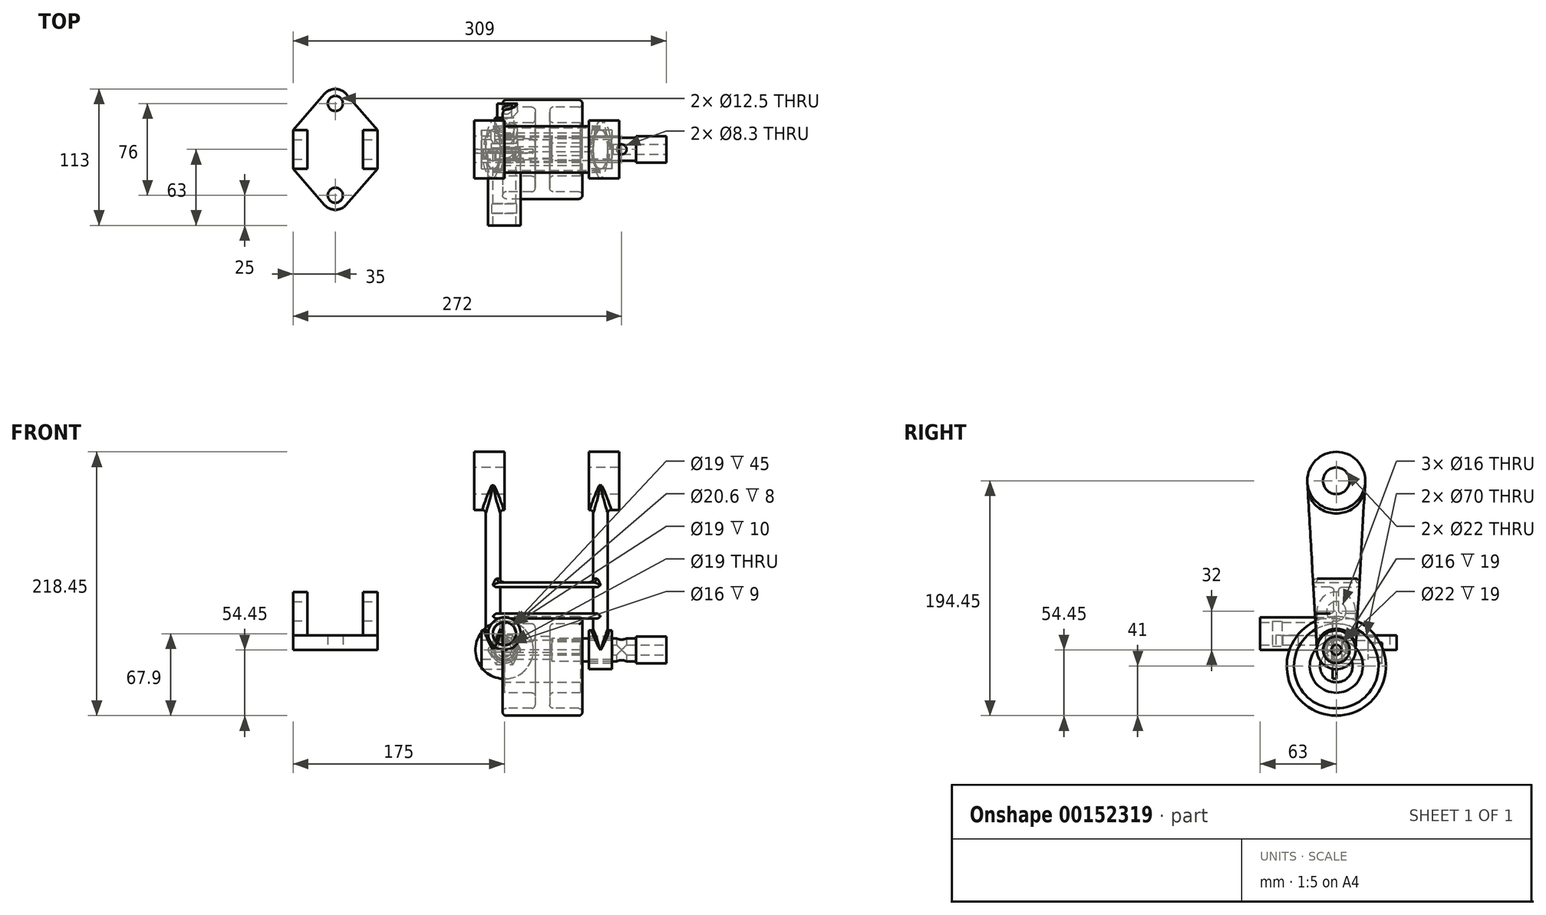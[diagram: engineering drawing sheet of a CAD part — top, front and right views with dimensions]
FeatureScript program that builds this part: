
annotation { "Feature Type Name" : "Feature", "Feature Type Description" : "" }
export const myFeature = defineFeature(function(context is Context, id is Id, definition is map)
    precondition{}
    {
        {
            assignVariable(context, id + "F0", {"name" : "gap", "anyValue" : 70});
        }
        {
            var Q0;
            Q0=qCreatedBy(makeId("Right.planeOp"),FACE);
            var sketch = newSketch(context, id + "F1", { "sketchPlane" : qUnion([Q0])});
            skCircle(sketch, "E0", {"center": v(0, 0) * mm, "radius": 16 * mm});
            skCircle(sketch, "E1", {"center": v(0, 140) * mm, "radius": 24 * mm});
            skSolve(sketch);
        }
        {
            var Q0;
            Q0=makeQuery(id+"F1.imprint","IMPRINT",FACE,{"disambiguationData":[TD([[makeQuery(id+"F1.imprint","IMPRINT",EDGE,{"derivedFrom":sQuery(id+"F1.wireOp",EDGE,"E1")}),1.0]])]});
            extrude(context, id + "F2", {"entities" : qUnion([Q0]), "oppositeDirection" : true, "depth" : 25 * mm});
        }
        {
            var Q0;
            Q0=makeQuery(id+"F1.imprint","IMPRINT",FACE,{"disambiguationData":[TD([[makeQuery(id+"F1.imprint","IMPRINT",EDGE,{"derivedFrom":sQuery(id+"F1.wireOp",EDGE,"E0")}),1.0]])]});
            extrude(context, id + "F3", {"entities" : qUnion([Q0]), "oppositeDirection" : true, "depth" : 19 * mm});
        }
        {
            var Q0;
            Q0=qCreatedBy(makeId("Top.planeOp"),FACE);
            var sketch = newSketch(context, id + "F4", { "sketchPlane" : qUnion([Q0])});
            skEllipse(sketch, "E2", {"center": v(-9.5, 0) * mm, "majorRadius": 16 * mm, "minorRadius": 6 * mm, "majorAxis": v(0, 1)});
            skLineSegment(sketch, "E3", {"start": v(-19, 16) * mm, "end": v(0, 16) * mm, "construction": true});
            skPoint(sketch, "E4", {"position": v(-15.5, 0) * mm});
            skSolve(sketch);
        }
        {
            var Q0;
            Q0=sQuery(id+"F1.wireOp",VERTEX,"E1.center");
            var Q1;
            Q1=qCreatedBy(makeId("Top.planeOp"),FACE);
            cPlane(context, id + "F5", {"entities" : qUnion([Q0, Q1]), "cplaneType" : CPlaneType.PLANE_POINT, "offset" : 25 * mm, "width" : 150 * mm, "height" : 150 * mm});
        }
        {
            var Q0;
            Q0=qCreatedBy(id+"F5.planeOp",FACE);
            var sketch = newSketch(context, id + "F6", { "sketchPlane" : qUnion([Q0])});
            skLineSegment(sketch, "E5", {"start": v(-25, 24) * mm, "end": v(0, 24) * mm, "construction": true});
            skEllipse(sketch, "E6", {"center": v(-9.5, 0) * mm, "majorRadius": 24 * mm, "minorRadius": 6 * mm, "majorAxis": v(0, 1)});
            skSolve(sketch);
        }
        {
            var Q2;
            Q2=qSketchRegion(id+"F6",true);
            var Q3;
            Q3=qSketchRegion(id+"F4",true);
            loft(context, id + "F7", {"operationType" : NewBodyOperationType.ADD, "sheetProfilesArray" : [{ "sheetProfileEntities" : qUnion([Q2]) }, { "sheetProfileEntities" : qUnion([Q3]) }]});
        }
        {
            var Q0;
            Q0=makeQuery(id+"F2.opExtrude","SWEPT_BODY",BODY,{"disambiguationData":[OSD([sQuery(id+"F1.wireOp",EDGE,"E1")])]});
            transform(context, id + "F8", {"entities" : qUnion([Q0]), "transformType" : TransformType.TRANSLATION_3D, "dx" : (getVariable(context, 'gap')) * mm, "dy" : 0 * mm, "dz" : 0 * mm, "makeCopy" : true});
        }
        {
            var Q0;
            Q0=makeQuery(id+"F8.opPattern","COPY",FACE,{"derivedFrom":makeQuery(id+"F2.opExtrude","CAP_FACE",FACE,{"disambiguationData":[OSD([sQuery(id+"F1.wireOp",EDGE,"E1")])],"isStart":true}),"instanceName":"1"});
            var sketch = newSketch(context, id + "F9", { "sketchPlane" : qUnion([Q0])});
            skLineSegment(sketch, "E7", {"start": v(0, 140) * mm, "end": v(0, -24.66) * mm, "construction": true});
            skSolve(sketch);
        }
        {
            var Q0;
            Q0=makeQuery(id+"F8.opPattern","COPY",BODY,{"derivedFrom":makeQuery(id+"F2.opExtrude","SWEPT_BODY",BODY,{"disambiguationData":[OSD([sQuery(id+"F1.wireOp",EDGE,"E1")])]}),"instanceName":"1"});
            var Q1;
            Q1=sQuery(id+"F9.wireOp",EDGE,"E7");
            transform(context, id + "F10", {"entities" : qUnion([Q0]), "transformType" : TransformType.ROTATION, "transformAxis" : qUnion([Q1]), "angle" : 180 * degree, "makeCopy" : false});
        }
        {
            var Q0;
            Q0=qCreatedBy(makeId("Right.planeOp"),FACE);
            cPlane(context, id + "F11", {"entities" : qUnion([Q0]), "cplaneType" : CPlaneType.OFFSET, "offset" : 9.5 * mm, "oppositeDirection" : true, "width" : 150 * mm, "height" : 150 * mm});
        }
        {
            var Q0;
            Q0=qCreatedBy(id+"F11.planeOp",FACE);
            var sketch = newSketch(context, id + "F12", { "sketchPlane" : qUnion([Q0])});
            skCircle(sketch, "E8.0", {"center": v(0, 140) * mm, "radius": 24 * mm, "construction": true});
            skCircle(sketch, "E9.0", {"center": v(0, 0) * mm, "radius": 16 * mm, "construction": true});
            skLineSegment(sketch, "E10", {"start": v(-23.96, 138.63) * mm, "end": v(-15.97, -0.91) * mm, "construction": true});
            skLineSegment(sketch, "E11", {"start": v(23.96, 138.63) * mm, "end": v(15.97, -0.91) * mm, "construction": true});
            skLineSegment(sketch, "E12", {"start": v(15.63, 26) * mm, "end": v(-15.63, 26) * mm});
            skArc(sketch, "E13", {"start": v(-15.63, 30) * mm, "mid": v(-17.63, 28) * mm, "end": v(-15.63, 26) * mm});
            skArc(sketch, "E14", {"start": v(15.63, 26) * mm, "mid": v(17.63, 28) * mm, "end": v(15.63, 30) * mm});
            skLineSegment(sketch, "E15", {"start": v(-17.11, 56) * mm, "end": v(17.11, 56) * mm});
            skArc(sketch, "E16", {"start": v(-17.11, 56) * mm, "mid": v(-19.11, 54) * mm, "end": v(-17.11, 52) * mm});
            skArc(sketch, "E17", {"start": v(17.11, 52) * mm, "mid": v(19.11, 54) * mm, "end": v(17.11, 56) * mm});
            skLineSegment(sketch, "E18", {"start": v(-17.11, 52) * mm, "end": v(-5, 52) * mm});
            skLineSegment(sketch, "E19", {"start": v(-2, 49) * mm, "end": v(-2, 33) * mm});
            skLineSegment(sketch, "E20", {"start": v(-5, 30) * mm, "end": v(-15.63, 30) * mm});
            skLineSegment(sketch, "E21", {"start": v(17.11, 52) * mm, "end": v(5, 52) * mm});
            skLineSegment(sketch, "E22", {"start": v(2, 49) * mm, "end": v(2, 33) * mm});
            skLineSegment(sketch, "E23", {"start": v(5, 30) * mm, "end": v(15.63, 30) * mm});
            skPoint(sketch, "E24.visualSharp", {"position": v(-2, 52) * mm});
            skArc(sketch, "E24.filletArc", {"start": v(-2, 49) * mm, "mid": v(-2.88, 51.12) * mm, "end": v(-5, 52) * mm});
            skPoint(sketch, "E25.visualSharp", {"position": v(2, 52) * mm});
            skArc(sketch, "E25.filletArc", {"start": v(5, 52) * mm, "mid": v(2.88, 51.12) * mm, "end": v(2, 49) * mm});
            skPoint(sketch, "E26.visualSharp", {"position": v(2, 30) * mm});
            skArc(sketch, "E26.filletArc", {"start": v(2, 33) * mm, "mid": v(2.88, 30.88) * mm, "end": v(5, 30) * mm});
            skPoint(sketch, "E27.visualSharp", {"position": v(-2, 30) * mm});
            skArc(sketch, "E27.filletArc", {"start": v(-5, 30) * mm, "mid": v(-2.88, 30.88) * mm, "end": v(-2, 33) * mm});
            skSolve(sketch);
        }
        {
            var Q0;
            Q0=qSketchRegion(id+"F12",true);
            var Q1;
            Q1=makeQuery(id+"F8.opPattern","COPY",BODY,{"derivedFrom":makeQuery(id+"F2.opExtrude","SWEPT_BODY",BODY,{"disambiguationData":[OSD([sQuery(id+"F1.wireOp",EDGE,"E1")])]}),"instanceName":"1"});
            extrude(context, id + "F13", {"entities" : qUnion([Q0]), "operationType" : NewBodyOperationType.ADD, "endBoundEntityBody" : qUnion([Q1]), "depth" : (getVariable(context, 'gap') + 19) * mm});
        }
        {
            var Q0;
            Q0=qCreatedBy(makeId("Top.planeOp"),FACE);
            var sketch = newSketch(context, id + "F14", { "sketchPlane" : qUnion([Q0])});
            skLineSegment(sketch, "E28", {"start": v(-175, 16) * mm, "end": v(-149.06, 45.87) * mm});
            skLineSegment(sketch, "E29", {"start": v(-130.94, 45.87) * mm, "end": v(-105, 16) * mm});
            skLineSegment(sketch, "E30", {"start": v(-105, -16) * mm, "end": v(-130.94, -45.87) * mm});
            skLineSegment(sketch, "E31", {"start": v(-149.06, -45.87) * mm, "end": v(-175, -16) * mm});
            skLineSegment(sketch, "E32", {"start": v(-175, 16) * mm, "end": v(-175, -16) * mm});
            skLineSegment(sketch, "E33", {"start": v(-105, 16) * mm, "end": v(-105, -16) * mm});
            skArc(sketch, "E34", {"start": v(-130.94, 45.87) * mm, "mid": v(-140, 50) * mm, "end": v(-149.06, 45.87) * mm});
            skArc(sketch, "E35", {"start": v(-149.06, -45.87) * mm, "mid": v(-140, -50) * mm, "end": v(-130.94, -45.87) * mm});
            skCircle(sketch, "E36", {"center": v(-140, 38) * mm, "radius": 6.25 * mm});
            skCircle(sketch, "E37", {"center": v(-140, -38) * mm, "radius": 6.25 * mm});
            skSolve(sketch);
        }
        {
            var Q0;
            Q0=makeQuery(id+"F2.opExtrude","CAP_FACE",FACE,{"disambiguationData":[OSD([sQuery(id+"F1.wireOp",EDGE,"E1")])],"isStart":false});
            var sketch = newSketch(context, id + "F15", { "sketchPlane" : qUnion([Q0])});
            skCircle(sketch, "E38", {"center": v(0, 140) * mm, "radius": 11 * mm});
            skCircle(sketch, "E39", {"center": v(0, 0) * mm, "radius": 8 * mm});
            skSolve(sketch);
        }
        {
            var Q0;
            Q0=qSketchRegion(id+"F15",true);
            extrude(context, id + "F16", {"entities" : qUnion([Q0]), "operationType" : NewBodyOperationType.REMOVE, "endBound" : BoundingType.THROUGH_ALL, "oppositeDirection" : true, "depth" : 25 * mm});
        }
        {
            var Q0;
            Q0=makeQuery(id+"F13.boolean.opBoolean","INTERSECT",EDGE,{"derivedFrom":[makeQuery(id+"F7.opLoft","SWEPT_FACE",FACE,{"disambiguationData":[OSD([sQuery(id+"F4.wireOp",EDGE,"E2"),sQuery(id+"F6.wireOp",EDGE,"E6")])]}),makeQuery(id+"F13.opExtrude","SWEPT_FACE",FACE,{"disambiguationData":[OSD([sQuery(id+"F12.wireOp",EDGE,"E15")])]})]});
            var Q1;
            Q1=makeQuery(id+"F13.boolean.opBoolean","INTERSECT",EDGE,{"derivedFrom":[makeQuery(id+"F8.opPattern","COPY",FACE,{"derivedFrom":makeQuery(id+"F7.opLoft","SWEPT_FACE",FACE,{"disambiguationData":[OSD([sQuery(id+"F4.wireOp",EDGE,"E2"),sQuery(id+"F6.wireOp",EDGE,"E6")])]}),"instanceName":"1"}),makeQuery(id+"F13.opExtrude","SWEPT_FACE",FACE,{"disambiguationData":[OSD([sQuery(id+"F12.wireOp",EDGE,"E15")])]})]});
            var Q2;
            Q2=makeQuery(id+"F7.boolean.opBoolean","INTERSECT",EDGE,{"derivedFrom":[makeQuery(id+"F2.opExtrude","SWEPT_FACE",FACE,{"disambiguationData":[OSD([sQuery(id+"F1.wireOp",EDGE,"E1")])]}),makeQuery(id+"F7.opLoft","SWEPT_FACE",FACE,{"disambiguationData":[OSD([sQuery(id+"F4.wireOp",EDGE,"E2"),sQuery(id+"F6.wireOp",EDGE,"E6")])]})]});
            var Q3;
            Q3=makeQuery(id+"F8.opPattern","COPY",EDGE,{"derivedFrom":makeQuery(id+"F7.boolean.opBoolean","INTERSECT",EDGE,{"derivedFrom":[makeQuery(id+"F2.opExtrude","SWEPT_FACE",FACE,{"disambiguationData":[OSD([sQuery(id+"F1.wireOp",EDGE,"E1")])]}),makeQuery(id+"F7.opLoft","SWEPT_FACE",FACE,{"disambiguationData":[OSD([sQuery(id+"F4.wireOp",EDGE,"E2"),sQuery(id+"F6.wireOp",EDGE,"E6")])]})]}),"instanceName":"1"});
            fillet(context, id + "F17", {"entities" : qUnion([Q0, Q1, Q2, Q3]), "radius" : 3 * mm, "tangentPropagation" : true, "allowEdgeOverflow" : false});
        }
        {
            var Q0;
            Q0=makeQuery(id+"F8.opPattern","COPY",EDGE,{"derivedFrom":makeQuery(id+"F7.boolean.opBoolean","INTERSECT",EDGE,{"derivedFrom":[makeQuery(id+"F3.opExtrude","SWEPT_FACE",FACE,{"disambiguationData":[OSD([sQuery(id+"F1.wireOp",EDGE,"E0")])]}),makeQuery(id+"F7.opLoft","SWEPT_FACE",FACE,{"disambiguationData":[OSD([sQuery(id+"F4.wireOp",EDGE,"E2"),sQuery(id+"F6.wireOp",EDGE,"E6")])]})]}),"instanceName":"1"});
            var Q1;
            Q1=makeQuery(id+"F7.boolean.opBoolean","INTERSECT",EDGE,{"derivedFrom":[makeQuery(id+"F3.opExtrude","SWEPT_FACE",FACE,{"disambiguationData":[OSD([sQuery(id+"F1.wireOp",EDGE,"E0")])]}),makeQuery(id+"F7.opLoft","SWEPT_FACE",FACE,{"disambiguationData":[OSD([sQuery(id+"F4.wireOp",EDGE,"E2"),sQuery(id+"F6.wireOp",EDGE,"E6")])]})]});
            fillet(context, id + "F18", {"entities" : qUnion([Q0, Q1]), "radius" : 1.5 * mm, "tangentPropagation" : true, "allowEdgeOverflow" : false});
        }
        {
            var Q0;
            Q0=qCreatedBy(makeId("Front.planeOp"),FACE);
            var sketch = newSketch(context, id + "F19", { "sketchPlane" : qUnion([Q0])});
            skLineSegment(sketch, "E40", {"start": v(0, 0) * mm, "end": v(63, 0) * mm});
            skLineSegment(sketch, "E41", {"start": v(63, 0) * mm, "end": v(63, 8.55) * mm});
            skLineSegment(sketch, "E42", {"start": v(63, 8.55) * mm, "end": v(40.5, 8.55) * mm});
            skLineSegment(sketch, "E43", {"start": v(37.5, 11.55) * mm, "end": v(37.5, 18.55) * mm});
            skLineSegment(sketch, "E44", {"start": v(40.5, 21.55) * mm, "end": v(61.5, 21.55) * mm});
            skArc(sketch, "E45", {"start": v(61.5, 21.55) * mm, "mid": v(64.5, 24.55) * mm, "end": v(61.5, 27.55) * mm});
            skLineSegment(sketch, "E46", {"start": v(61.5, 27.55) * mm, "end": v(1.5, 27.55) * mm});
            skArc(sketch, "E47", {"start": v(1.5, 27.55) * mm, "mid": v(-1.5, 24.55) * mm, "end": v(1.5, 21.55) * mm});
            skLineSegment(sketch, "E48", {"start": v(1.5, 21.55) * mm, "end": v(22.5, 21.55) * mm});
            skLineSegment(sketch, "E49", {"start": v(25.5, 18.55) * mm, "end": v(25.5, 11.55) * mm});
            skLineSegment(sketch, "E50", {"start": v(22.5, 8.55) * mm, "end": v(0, 8.55) * mm});
            skLineSegment(sketch, "E51", {"start": v(0, 8.55) * mm, "end": v(0, 0) * mm});
            skPoint(sketch, "E52.visualSharp", {"position": v(37.5, 8.55) * mm});
            skArc(sketch, "E52.filletArc", {"start": v(37.5, 11.55) * mm, "mid": v(38.38, 9.43) * mm, "end": v(40.5, 8.55) * mm});
            skPoint(sketch, "E53.visualSharp", {"position": v(25.5, 8.55) * mm});
            skArc(sketch, "E53.filletArc", {"start": v(22.5, 8.55) * mm, "mid": v(24.62, 9.43) * mm, "end": v(25.5, 11.55) * mm});
            skLineSegment(sketch, "E54", {"start": v(0, -13.45) * mm, "end": v(71.85, -13.45) * mm, "construction": true});
            skPoint(sketch, "E55.visualSharp", {"position": v(25.5, 21.55) * mm});
            skArc(sketch, "E55.filletArc", {"start": v(25.5, 18.55) * mm, "mid": v(24.62, 20.67) * mm, "end": v(22.5, 21.55) * mm});
            skPoint(sketch, "E56.visualSharp", {"position": v(37.5, 21.55) * mm});
            skArc(sketch, "E56.filletArc", {"start": v(40.5, 21.55) * mm, "mid": v(38.38, 20.67) * mm, "end": v(37.5, 18.55) * mm});
            skSolve(sketch);
        }
        {
            var Q0;
            Q0=makeQuery(id+"F19.imprint","IMPRINT",FACE,{"disambiguationData":[TD([[makeQuery(id+"F19.imprint","IMPRINT",EDGE,{"derivedFrom":sQuery(id+"F19.wireOp",EDGE,"E40")}),1.0]])]});
            var Q1;
            Q1=sQuery(id+"F19.wireOp",EDGE,"E54");
            revolve(context, id + "F20", {"entities" : qUnion([Q0]), "axis" : qUnion([Q1]), "revolveType" : RevolveType.FULL});
        }
        {
            var Q0;
            Q0=qCreatedBy(makeId("Right.planeOp"),FACE);
            var sketch = newSketch(context, id + "F21", { "sketchPlane" : qUnion([Q0])});
            skLineSegment(sketch, "E57", {"start": v(0, 0) * mm, "end": v(-63, 0) * mm});
            skLineSegment(sketch, "E58", {"start": v(-63, 0) * mm, "end": v(-63, 3.95) * mm});
            skLineSegment(sketch, "E59", {"start": v(-63, 3.95) * mm, "end": v(-53, 3.95) * mm});
            skLineSegment(sketch, "E60", {"start": v(-53, 3.95) * mm, "end": v(-53, 3.15) * mm});
            skLineSegment(sketch, "E61", {"start": v(-53, 3.15) * mm, "end": v(-45, 3.15) * mm});
            skLineSegment(sketch, "E62", {"start": v(-45, 3.15) * mm, "end": v(-45, 3.95) * mm});
            skLineSegment(sketch, "E63", {"start": v(-45, 3.95) * mm, "end": v(0, 3.95) * mm});
            skLineSegment(sketch, "E64", {"start": v(0, 3.95) * mm, "end": v(0, 0) * mm});
            skLineSegment(sketch, "E65", {"start": v(0, 13.45) * mm, "end": v(-63, 13.45) * mm, "construction": true});
            skPoint(sketch, "E65.startSnap0", {"position": v(0, 1.98) * mm});
            skSolve(sketch);
        }
        {
            var Q0;
            Q0=makeQuery(id+"F21.imprint","IMPRINT",FACE,{"disambiguationData":[TD([[makeQuery(id+"F21.imprint","IMPRINT",EDGE,{"derivedFrom":sQuery(id+"F21.wireOp",EDGE,"E57")}),-1.0]])]});
            var Q1;
            Q1=sQuery(id+"F21.wireOp",EDGE,"E65");
            revolve(context, id + "F22", {"entities" : qUnion([Q0]), "axis" : qUnion([Q1]), "revolveType" : RevolveType.FULL});
        }
        {
            var Q0;
            Q0=qSketchRegion(id+"F14",true);
            extrude(context, id + "F23", {"entities" : qUnion([Q0]), "depth" : 12 * mm});
        }
        {
            var Q0;
            Q0=qCreatedBy(makeId("Right.planeOp"),FACE);
            var sketch = newSketch(context, id + "F24", { "sketchPlane" : qUnion([Q0])});
            skCircle(sketch, "E66", {"center": v(0, 0) * mm, "radius": 11 * mm});
            skSolve(sketch);
        }
        {
            var Q0;
            Q0=qSketchRegion(id+"F24",true);
            extrude(context, id + "F25", {"entities" : qUnion([Q0]), "depth" : 134 * mm});
        }
        {
            var Q0;
            Q0=makeQuery(id+"F25.opExtrude","CAP_FACE",FACE,{"disambiguationData":[OSD([sQuery(id+"F24.wireOp",EDGE,"E66")])],"isStart":false});
            var sketch = newSketch(context, id + "F26", { "sketchPlane" : qUnion([Q0])});
            skCircle(sketch, "E67", {"center": v(0, 0) * mm, "radius": 4.15 * mm});
            skSolve(sketch);
        }
        {
            var Q0;
            Q0=qSketchRegion(id+"F26",true);
            extrude(context, id + "F27", {"entities" : qUnion([Q0]), "operationType" : NewBodyOperationType.REMOVE, "oppositeDirection" : true, "depth" : 44 * mm});
        }
        {
            var Q0;
            Q0=qCreatedBy(makeId("Top.planeOp"),FACE);
            var sketch = newSketch(context, id + "F28", { "sketchPlane" : qUnion([Q0])});
            skCircle(sketch, "E68", {"center": v(97, 0) * mm, "radius": 4.15 * mm});
            skSolve(sketch);
        }
        {
            var Q0;
            Q0=qSketchRegion(id+"F28",true);
            extrude(context, id + "F29", {"entities" : qUnion([Q0]), "operationType" : NewBodyOperationType.REMOVE, "endBound" : BoundingType.SYMMETRIC, "depth" : 25 * mm});
        }
        {
            var Q0;
            Q0=makeQuery(id+"F25.opExtrude","CAP_FACE",FACE,{"disambiguationData":[OSD([sQuery(id+"F24.wireOp",EDGE,"E66")])],"isStart":true});
            var sketch = newSketch(context, id + "F30", { "sketchPlane" : qUnion([Q0])});
            skCircle(sketch, "E69", {"center": v(0, 0) * mm, "radius": 9.5 * mm});
            skSolve(sketch);
        }
        {
            var Q0;
            Q0=makeQuery(id+"F30.imprint","IMPRINT",FACE,{"disambiguationData":[TD([[makeQuery(id+"F30.imprint","IMPRINT",EDGE,{"derivedFrom":sQuery(id+"F30.wireOp",EDGE,"E69")}),-1.0]])]});
            extrude(context, id + "F31", {"entities" : qUnion([Q0]), "operationType" : NewBodyOperationType.REMOVE, "oppositeDirection" : true, "depth" : 109 * mm});
        }
        {
            var Q0;
            Q0=makeQuery(id+"F25.opExtrude","CAP_FACE",FACE,{"disambiguationData":[OSD([sQuery(id+"F24.wireOp",EDGE,"E66")])],"isStart":true});
            var sketch = newSketch(context, id + "F32", { "sketchPlane" : qUnion([Q0])});
            skCircle(sketch, "E70", {"center": v(0, 0) * mm, "radius": 8 * mm});
            skSolve(sketch);
        }
        {
            var Q0;
            Q0=makeQuery(id+"F32.imprint","IMPRINT",FACE,{"disambiguationData":[TD([[makeQuery(id+"F32.imprint","IMPRINT",EDGE,{"derivedFrom":sQuery(id+"F32.wireOp",EDGE,"E70")}),-1.0]])]});
            extrude(context, id + "F33", {"entities" : qUnion([Q0]), "operationType" : NewBodyOperationType.REMOVE, "oppositeDirection" : true, "depth" : 39 * mm});
        }
        {
            var Q0;
            Q0=qCreatedBy(makeId("Front.planeOp"),FACE);
            var sketch = newSketch(context, id + "F34", { "sketchPlane" : qUnion([Q0])});
            skCircle(sketch, "E71", {"center": v(0, 0) * mm, "radius": 24 * mm});
            skCircle(sketch, "E72", {"center": v(0, 0) * mm, "radius": 9.5 * mm});
            skSolve(sketch);
        }
        {
            var Q0;
            Q0=makeQuery(id+"F34.imprint","IMPRINT",FACE,{"disambiguationData":[TD([[makeQuery(id+"F34.imprint","IMPRINT",EDGE,{"derivedFrom":sQuery(id+"F34.wireOp",EDGE,"E71")}),1.0]])]});
            extrude(context, id + "F35", {"entities" : qUnion([Q0]), "depth" : 3 * mm});
        }
        {
            var Q0;
            Q0=qCreatedBy(makeId("Front.planeOp"),FACE);
            var sketch = newSketch(context, id + "F36", { "sketchPlane" : qUnion([Q0])});
            skCircle(sketch, "E73.cCircle", {"center": v(0, 0) * mm, "radius": 12 * mm, "construction": true});
            skLineSegment(sketch, "E73.0", {"start": v(6.93, 12) * mm, "end": v(13.86, 0) * mm});
            skLineSegment(sketch, "E73.1", {"start": v(13.86, 0) * mm, "end": v(6.93, -12) * mm});
            skLineSegment(sketch, "E73.2", {"start": v(6.93, -12) * mm, "end": v(-6.93, -12) * mm});
            skLineSegment(sketch, "E73.3", {"start": v(-6.93, -12) * mm, "end": v(-13.86, 0) * mm});
            skLineSegment(sketch, "E73.4", {"start": v(-13.86, 0) * mm, "end": v(-6.93, 12) * mm});
            skLineSegment(sketch, "E73.5", {"start": v(-6.93, 12) * mm, "end": v(6.93, 12) * mm});
            skPoint(sketch, "E73.0.midPoint", {"position": v(10.4, 6) * mm});
            skCircle(sketch, "E74", {"center": v(0, 0) * mm, "radius": 8 * mm});
            skSolve(sketch);
        }
        {
            var Q0;
            Q0=makeQuery(id+"F36.imprint","IMPRINT",FACE,{"disambiguationData":[TD([[makeQuery(id+"F36.imprint","IMPRINT",EDGE,{"derivedFrom":sQuery(id+"F36.wireOp",EDGE,"E73.0")}),-1.0]])]});
            extrude(context, id + "F37", {"entities" : qUnion([Q0]), "depth" : 9 * mm});
        }
        {
            var Q0;
            Q0=makeQuery(id+"F37.opExtrude","CAP_EDGE",EDGE,{"disambiguationData":[OSD([sQuery(id+"F36.wireOp",EDGE,"E73.5")])],"isStart":true});
            var Q1;
            Q1=makeQuery(id+"F37.opExtrude","CAP_EDGE",EDGE,{"disambiguationData":[OSD([sQuery(id+"F36.wireOp",EDGE,"E73.0")])],"isStart":true});
            var Q2;
            Q2=makeQuery(id+"F37.opExtrude","CAP_EDGE",EDGE,{"disambiguationData":[OSD([sQuery(id+"F36.wireOp",EDGE,"E73.1")])],"isStart":true});
            var Q3;
            Q3=makeQuery(id+"F37.opExtrude","CAP_EDGE",EDGE,{"disambiguationData":[OSD([sQuery(id+"F36.wireOp",EDGE,"E73.2")])],"isStart":true});
            var Q4;
            Q4=makeQuery(id+"F37.opExtrude","CAP_EDGE",EDGE,{"disambiguationData":[OSD([sQuery(id+"F36.wireOp",EDGE,"E73.3")])],"isStart":true});
            var Q5;
            Q5=makeQuery(id+"F37.opExtrude","CAP_EDGE",EDGE,{"disambiguationData":[OSD([sQuery(id+"F36.wireOp",EDGE,"E73.4")])],"isStart":true});
            chamfer(context, id + "F38", {"entities" : qUnion([Q0, Q1, Q2, Q3, Q4, Q5]), "chamferType" : ChamferType.OFFSET_ANGLE, "width" : 3 * mm, "oppositeDirection" : false, "angle" : 30 * degree, "tangentPropagation" : true});
        }
        {
            var Q0;
            Q0=qCreatedBy(makeId("Front.planeOp"),FACE);
            var sketch = newSketch(context, id + "F39", { "sketchPlane" : qUnion([Q0])});
            skCircle(sketch, "E75", {"center": v(0, 0) * mm, "radius": 11 * mm});
            skSolve(sketch);
        }
        {
            var Q0;
            Q0=qSketchRegion(id+"F39",true);
            extrude(context, id + "F40", {"entities" : qUnion([Q0]), "oppositeDirection" : true, "depth" : 38 * mm});
        }
        {
            var Q0;
            Q0=makeQuery(id+"F40.opExtrude","CAP_EDGE",EDGE,{"disambiguationData":[OSD([sQuery(id+"F39.wireOp",EDGE,"E75")])],"isStart":true});
            fillet(context, id + "F41", {"entities" : qUnion([Q0]), "radius" : 1.5 * mm, "tangentPropagation" : true, "allowEdgeOverflow" : false});
        }
        {
            var Q0;
            Q0=makeQuery(id+"F40.opExtrude","CAP_FACE",FACE,{"disambiguationData":[OSD([sQuery(id+"F39.wireOp",EDGE,"E75")])],"isStart":false});
            var sketch = newSketch(context, id + "F42", { "sketchPlane" : qUnion([Q0])});
            skCircle(sketch, "E76", {"center": v(0, 0) * mm, "radius": 8 * mm});
            skSolve(sketch);
        }
        {
            var Q0;
            Q0=makeQuery(id+"F42.imprint","IMPRINT",FACE,{"disambiguationData":[TD([[makeQuery(id+"F42.imprint","IMPRINT",EDGE,{"derivedFrom":sQuery(id+"F42.wireOp",EDGE,"E76")}),-1.0]])]});
            extrude(context, id + "F43", {"entities" : qUnion([Q0]), "operationType" : NewBodyOperationType.REMOVE, "oppositeDirection" : true, "depth" : 33 * mm});
        }
        {
            var Q0;
            Q0=makeQuery(id+"F40.opExtrude","CAP_FACE",FACE,{"disambiguationData":[OSD([sQuery(id+"F39.wireOp",EDGE,"E75")])],"isStart":false});
            var sketch = newSketch(context, id + "F44", { "sketchPlane" : qUnion([Q0])});
            skCircle(sketch, "E77", {"center": v(0, 0) * mm, "radius": 6 * mm});
            skSolve(sketch);
        }
        {
            var Q0;
            Q0=makeQuery(id+"F44.imprint","IMPRINT",FACE,{"disambiguationData":[TD([[makeQuery(id+"F44.imprint","IMPRINT",EDGE,{"derivedFrom":sQuery(id+"F44.wireOp",EDGE,"E77")}),-1.0]])]});
            extrude(context, id + "F45", {"entities" : qUnion([Q0]), "operationType" : NewBodyOperationType.REMOVE, "oppositeDirection" : true, "depth" : 12 * mm});
        }
        {
            var Q0;
            Q0=makeQuery(id+"F40.opExtrude","CAP_FACE",FACE,{"disambiguationData":[OSD([sQuery(id+"F39.wireOp",EDGE,"E75")])],"isStart":true});
            var sketch = newSketch(context, id + "F46", { "sketchPlane" : qUnion([Q0])});
            skLineSegment(sketch, "E78.bottom", {"start": v(-12.48, 1.5) * mm, "end": v(12.63, 1.5) * mm});
            skLineSegment(sketch, "E78.top", {"start": v(-12.48, -1.5) * mm, "end": v(12.63, -1.5) * mm});
            skLineSegment(sketch, "E78.left", {"start": v(-12.48, 1.5) * mm, "end": v(-12.48, -1.5) * mm});
            skLineSegment(sketch, "E78.right", {"start": v(12.63, 1.5) * mm, "end": v(12.63, -1.5) * mm});
            skSolve(sketch);
        }
        {
            var Q0;
            Q0=qSketchRegion(id+"F46",true);
            extrude(context, id + "F47", {"entities" : qUnion([Q0]), "operationType" : NewBodyOperationType.REMOVE, "oppositeDirection" : true, "depth" : 1.5 * mm});
        }
        {
            var Q0;
            Q0=makeQuery(id+"F23.opExtrude","SWEPT_FACE",FACE,{"disambiguationData":[OSD([sQuery(id+"F14.wireOp",EDGE,"E33")])]});
            cPlane(context, id + "F48", {"entities" : qUnion([Q0]), "cplaneType" : CPlaneType.OFFSET, "offset" : 1 * mm, "width" : 150 * mm, "height" : 150 * mm});
        }
        {
            var Q0;
            Q0=qCreatedBy(id+"F48.planeOp",FACE);
            var sketch = newSketch(context, id + "F49", { "sketchPlane" : qUnion([Q0])});
            skLineSegment(sketch, "E79", {"start": v(-16, 0) * mm, "end": v(-16, 32) * mm});
            skLineSegment(sketch, "E80", {"start": v(16, 0) * mm, "end": v(16, 32) * mm});
            skArc(sketch, "E81", {"start": v(16, 32) * mm, "mid": v(0, 48) * mm, "end": v(-16, 32) * mm});
            skLineSegment(sketch, "E82", {"start": v(-16, 0) * mm, "end": v(16, 0) * mm});
            skCircle(sketch, "E83", {"center": v(0, 32) * mm, "radius": 8 * mm});
            skSolve(sketch);
        }
        {
            var Q0;
            Q0=makeQuery(id+"F49.imprint","IMPRINT",FACE,{"disambiguationData":[TD([[makeQuery(id+"F49.imprint","IMPRINT",EDGE,{"derivedFrom":sQuery(id+"F49.wireOp",EDGE,"E79")}),-1.0]])]});
            extrude(context, id + "F50", {"entities" : qUnion([Q0]), "operationType" : NewBodyOperationType.ADD, "oppositeDirection" : true, "depth" : 71 * mm});
        }
        {
            var Q0;
            Q0=makeQuery(id+"F50.opExtrude","SWEPT_FACE",FACE,{"disambiguationData":[OSD([sQuery(id+"F49.wireOp",EDGE,"E79")])]});
            var sketch = newSketch(context, id + "F51", { "sketchPlane" : qUnion([Q0])});
            skLineSegment(sketch, "E84.bottom", {"start": v(-163, 48) * mm, "end": v(-117, 48) * mm});
            skLineSegment(sketch, "E84.top", {"start": v(-163, 12) * mm, "end": v(-117, 12) * mm});
            skLineSegment(sketch, "E84.left", {"start": v(-163, 48) * mm, "end": v(-163, 12) * mm});
            skLineSegment(sketch, "E84.right", {"start": v(-117, 48) * mm, "end": v(-117, 12) * mm});
            skLineSegment(sketch, "E85.bottom", {"start": v(-105, 48) * mm, "end": v(-104, 48) * mm});
            skLineSegment(sketch, "E85.top", {"start": v(-105, 0) * mm, "end": v(-104, 0) * mm});
            skLineSegment(sketch, "E85.left", {"start": v(-105, 48) * mm, "end": v(-105, 0) * mm});
            skLineSegment(sketch, "E85.right", {"start": v(-104, 48) * mm, "end": v(-104, 0) * mm});
            skSolve(sketch);
        }
        {
            var Q0;
            Q0=qSketchRegion(id+"F51",true);
            extrude(context, id + "F52", {"entities" : qUnion([Q0]), "operationType" : NewBodyOperationType.REMOVE, "endBound" : BoundingType.THROUGH_ALL, "oppositeDirection" : true, "depth" : 25 * mm});
        }
    });
